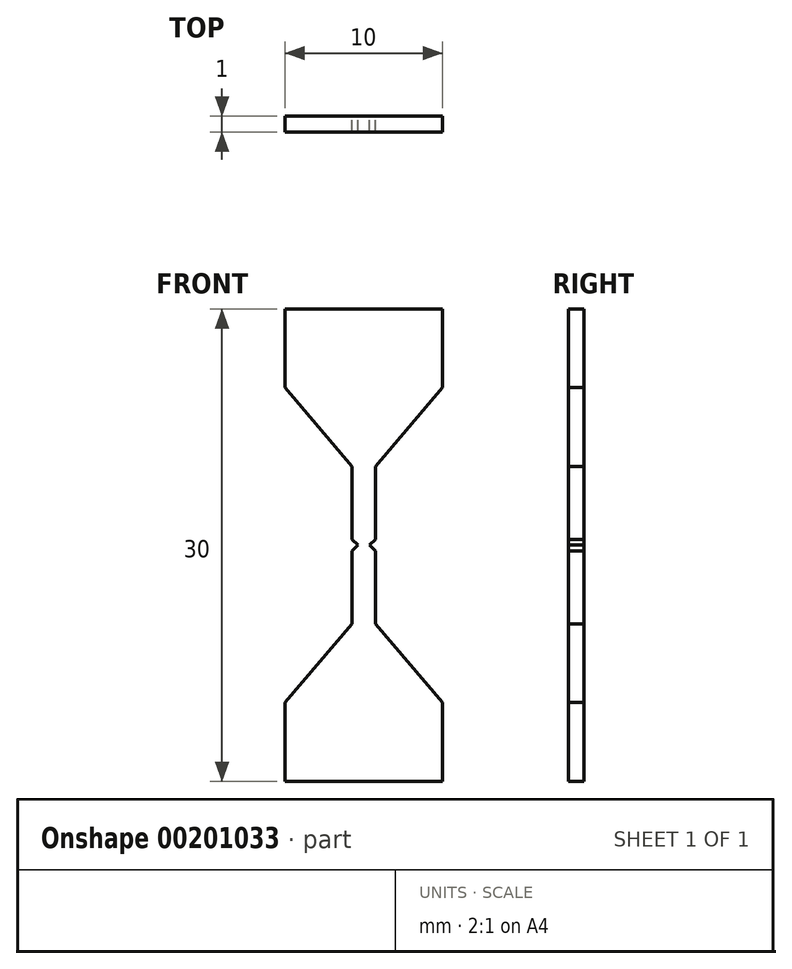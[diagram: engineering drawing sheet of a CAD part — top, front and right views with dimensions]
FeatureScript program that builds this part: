
annotation { "Feature Type Name" : "Feature", "Feature Type Description" : "" }
export const myFeature = defineFeature(function(context is Context, id is Id, definition is map)
    precondition{}
    {
        {
            var Q0;
            Q0=qCreatedBy(makeId("Front.planeOp"),FACE);
            var sketch = newSketch(context, id + "F0", { "sketchPlane" : qUnion([Q0])});
            skLineSegment(sketch, "E0.bottom", {"start": v(-5, 0) * mm, "end": v(5, 0) * mm});
            skLineSegment(sketch, "E0.top", {"start": v(-5, 5) * mm, "end": v(5, 5) * mm});
            skLineSegment(sketch, "E0.left", {"start": v(-5, 0) * mm, "end": v(-5, 5) * mm});
            skLineSegment(sketch, "E0.right", {"start": v(5, 0) * mm, "end": v(5, 5) * mm});
            skPoint(sketch, "E1", {"position": v(0, 5) * mm});
            skLineSegment(sketch, "E2", {"start": v(-0.75, 10) * mm, "end": v(0.75, 10) * mm});
            skLineSegment(sketch, "E3", {"start": v(-5, 5) * mm, "end": v(-0.75, 10) * mm});
            skLineSegment(sketch, "E4", {"start": v(0.75, 10) * mm, "end": v(5, 5) * mm});
            skPoint(sketch, "E5", {"position": v(0, 10) * mm});
            skLineSegment(sketch, "E6.top", {"start": v(-0.75, 15) * mm, "end": v(0, 15) * mm});
            skLineSegment(sketch, "E6.left", {"start": v(-0.75, 10) * mm, "end": v(-0.75, 15) * mm});
            skLineSegment(sketch, "E6.right", {"start": v(0.75, 10) * mm, "end": v(0.75, 15) * mm});
            skLineSegment(sketch, "E7.MirrorCS", {"start": v(0.75, 20) * mm, "end": v(0.75, 15) * mm});
            skLineSegment(sketch, "E8.MirrorCS", {"start": v(-0.75, 20) * mm, "end": v(0.75, 20) * mm});
            skLineSegment(sketch, "E9.MirrorCS", {"start": v(-5, 25) * mm, "end": v(-0.75, 20) * mm});
            skLineSegment(sketch, "E10.MirrorCS", {"start": v(0.75, 20) * mm, "end": v(5, 25) * mm});
            skLineSegment(sketch, "E11.MirrorCS", {"start": v(5, 30) * mm, "end": v(5, 25) * mm});
            skLineSegment(sketch, "E12.MirrorCS", {"start": v(-5, 30) * mm, "end": v(5, 30) * mm});
            skLineSegment(sketch, "E13.MirrorCS", {"start": v(-5, 30) * mm, "end": v(-5, 25) * mm});
            skLineSegment(sketch, "E14", {"start": v(0, 15) * mm, "end": v(0.75, 15) * mm});
            skPoint(sketch, "E15", {"position": v(-0.38, 15) * mm});
            skPoint(sketch, "E16", {"position": v(0.38, 15) * mm});
            skLineSegment(sketch, "E17.MirrorCS", {"start": v(-0.75, 20) * mm, "end": v(-0.75, 15) * mm});
            skLineSegment(sketch, "E18.bottom", {"start": v(-0.75, 15) * mm, "end": v(-0.38, 15) * mm});
            skLineSegment(sketch, "E18.top", {"start": v(-0.75, 15.38) * mm, "end": v(-0.38, 15.38) * mm});
            skLineSegment(sketch, "E18.left", {"start": v(-0.75, 15) * mm, "end": v(-0.75, 15.38) * mm});
            skLineSegment(sketch, "E18.right", {"start": v(-0.38, 15) * mm, "end": v(-0.38, 15.38) * mm});
            skLineSegment(sketch, "E19.MirrorCS", {"start": v(0.75, 15.38) * mm, "end": v(0.38, 15.38) * mm});
            skLineSegment(sketch, "E20.MirrorCS", {"start": v(-0.75, 14.62) * mm, "end": v(-0.38, 14.62) * mm});
            skLineSegment(sketch, "E21.MirrorCS", {"start": v(0.75, 14.62) * mm, "end": v(0.38, 14.62) * mm});
            skLineSegment(sketch, "E22", {"start": v(-0.75, 15.38) * mm, "end": v(-0.38, 15) * mm});
            skLineSegment(sketch, "E23", {"start": v(-0.75, 14.62) * mm, "end": v(-0.38, 15) * mm});
            skLineSegment(sketch, "E24", {"start": v(0.75, 15.38) * mm, "end": v(0.38, 15) * mm});
            skLineSegment(sketch, "E25", {"start": v(0.75, 14.62) * mm, "end": v(0.38, 15) * mm});
            skSolve(sketch);
        }
        {
            var Q0;
            {var subQ4=sQuery(id+"F0.wireOp",EDGE,"E8.MirrorCS");Q0=makeQuery(id+"F0.imprint","IMPRINT",FACE,{"disambiguationData":[TD([[makeQuery(id+"F0.imprint","IMPRINT",EDGE,{"derivedFrom":subQ4}),-1.0]])]});}
            var Q1;
            Q1=makeQuery(id+"F0.imprint","IMPRINT",FACE,{"disambiguationData":[TD([[makeQuery(id+"F0.imprint","IMPRINT",EDGE,{"derivedFrom":sQuery(id+"F0.wireOp",EDGE,"E0.bottom")}),1.0]])]});
            var Q2;
            Q2=makeQuery(id+"F0.imprint","IMPRINT",FACE,{"disambiguationData":[TD([[makeQuery(id+"F0.imprint","IMPRINT",EDGE,{"derivedFrom":sQuery(id+"F0.wireOp",EDGE,"E8.MirrorCS")}),1.0]])]});
            var Q3;
            Q3=makeQuery(id+"F0.imprint","IMPRINT",FACE,{"disambiguationData":[TD([[makeQuery(id+"F0.imprint","IMPRINT",EDGE,{"derivedFrom":sQuery(id+"F0.wireOp",EDGE,"E0.top")}),1.0]])]});
            var Q4;
            {var subQ1=sQuery(id+"F0.wireOp",EDGE,"E2");Q4=makeQuery(id+"F0.imprint","IMPRINT",FACE,{"disambiguationData":[TD([[makeQuery(id+"F0.imprint","IMPRINT",EDGE,{"derivedFrom":subQ1}),1.0]])]});}
            var Q5;
            Q5=makeQuery(id+"F0.imprint","IMPRINT",FACE,{"disambiguationData":[TD([[makeQuery(id+"F0.imprint","IMPRINT",EDGE,{"derivedFrom":sQuery(id+"F0.wireOp",EDGE,"E18.top")}),-1.0]])]});
            extrude(context, id + "F1", {"entities" : qUnion([Q0, Q1, Q2, Q3, Q4, Q5]), "depth" : 1 * mm});
        }
    });
